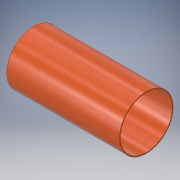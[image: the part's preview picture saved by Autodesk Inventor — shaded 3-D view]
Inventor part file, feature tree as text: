
AUTODESK INVENTOR PART (.ipt)
format: ipt  version: 2017 SP1 (Build 210196100, 196)  size: 108,544 bytes
history: native  units: in
note: dims shown in document units (in); Inventor stores cm internally (conversion verified against a paired STEP export)
features: extrude x1, sketch x1
ambient origin geometry x8: Origin, YZ Plane, XZ Plane, XY Plane, X Axis, Y Axis, Z Axis, Center Point
bodies: Solid1 (feature_tree)
feature tree (2):
  extrude  "Extrusion1"  Depth=15.0in
  sketch  "Sketch1"  dims[d0=7.15in d1=6.9in d2=15.0in d3=0.0in]
